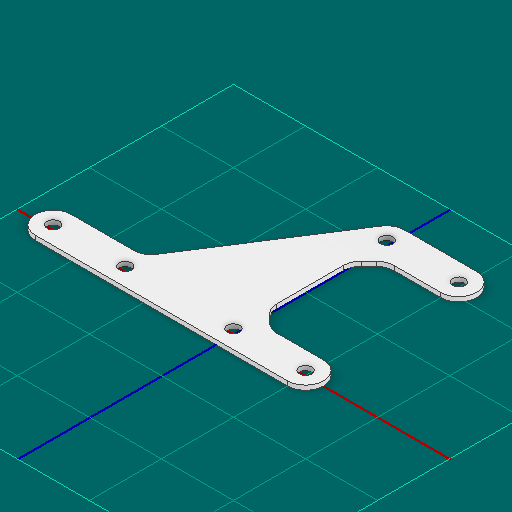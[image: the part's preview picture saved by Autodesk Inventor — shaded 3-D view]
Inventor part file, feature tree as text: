
AUTODESK INVENTOR PART (.ipt)
format: ipt  version: 2025 (Build 290162000, 162)  size: 130,560 bytes
history: native  units: in
note: dims shown in document units (in); Inventor stores cm internally (conversion verified against a paired STEP export)
features: other x3, extrude x1, sketch x1
ambient origin geometry x8: Origin, YZ Plane, XZ Plane, XY Plane, X Axis, Y Axis, Z Axis, Center Point
bodies: Solid1 (feature_tree)
feature tree (5):
  other  "Blocks"
  extrude  "Extrusion1"  Depth=0.25in
  sketch  "Sketch1"  dims[d0=0.25in d1=0.25in d2=0.0625in d3=0.0in]
  other  "main"
  other  "main:1"
